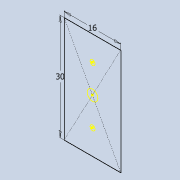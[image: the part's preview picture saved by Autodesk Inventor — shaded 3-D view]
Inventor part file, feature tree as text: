
AUTODESK INVENTOR PART (.ipt)
format: ipt  version: 2020 (Build 240168000, 168)  size: 143,360 bytes
history: native  units: mm
features: reference x8, other x6, extrude x3, sketch x3, plane x2, mirror x1, projected_geometry x1
ambient origin geometry x8: Origin, YZ Plane, XZ Plane, XY Plane, X Axis, Y Axis, Z Axis, Center Point
bodies: Solid1 (feature_tree)
feature tree (24):
  plane  "Work Plane1"
  extrude  "Extrusion1"  Depth=40.0mm
  plane  "Work Plane2"
  extrude  "Extrusion2"  Depth=3.0mm
  extrude  "Extrusion3"  Depth=10.0mm
  mirror  "Mirror1"
  sketch  "Sketch2"  dims[d2=26.0mm d3=40.0mm]
  reference  "Reference4"
  reference  "Reference5"
  reference  "Reference6"
  reference  "Reference7"
  sketch  "Sketch3"  dims[d4=6.0mm d5=3.0mm]
  reference  "Reference8"
  projected_geometry  "Projected Loop1"
  sketch  "Sketch4"  dims[d6=4.0mm d7=0.0mm d8=10.0mm d9=12.0mm d10=4.0mm d11=0.0mm d12=4.0mm d13=4.0mm d14=4.0mm d15=0.0mm]
  reference  "Reference9"
  reference  "Reference10"
  reference  "Reference11"
  parser-record x1  (decoder bookkeeping rows leaked as tree rows — omitted from the tree; the rows remain in map.json)
  other  "tip_3_n_base.iam"
  other  "bearing_hh_1:1"
  other  "bearing_hh_1:2"
  other  "pin3_40:1"
  other  "bearing_3_6_2:2"
note: 1 file-system path scrubbed to <path> (originals preserved in map.json)
